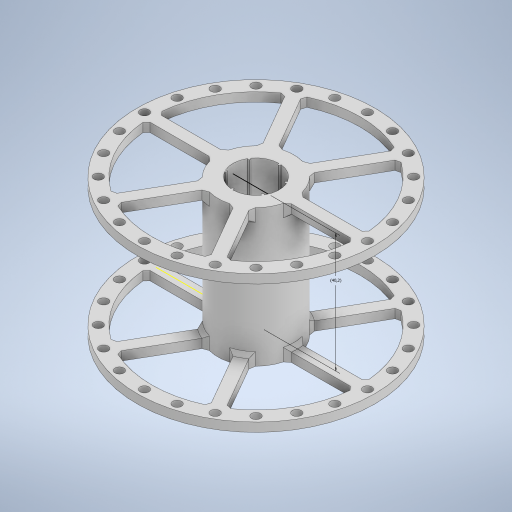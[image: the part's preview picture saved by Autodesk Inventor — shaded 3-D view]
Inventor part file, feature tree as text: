
AUTODESK INVENTOR PART (.ipt)
format: ipt  version: 2024 (Build 280153000, 153)  size: 560,128 bytes
history: native  units: mm
features: sketch x6, extrude x5, pattern_circular x3, chamfer x2, mirror x2, fillet x1
ambient origin geometry x8: Origin, YZ Plane, XZ Plane, XY Plane, X Axis, Y Axis, Z Axis, Center Point
bodies: Volumenkörper1 (feature_tree)
feature tree (19):
  extrude  "Extrusion1"  Depth=25.5mm
  extrude  "Extrusion2"  Depth=46.2mm
  extrude  "Extrusion4"  Depth=3.0mm TaperAngle=0.0deg
  chamfer  "Fasen1"  Distance=3.0mm
  mirror  "Spiegeln2"
  pattern_circular  "Runde Anordnung2"  Count=6 Angle=360.0deg
  chamfer  "Fasen2"  Distance=1.25mm Angle=45.0deg
  extrude  "Extrusion5"  Depth=3.0mm
  pattern_circular  "Runde Anordnung3"  [2 undecoded]
  mirror  "Spiegeln3"
  extrude  "Extrusion6"  Depth=0.35mm TaperAngle=360.0deg
  pattern_circular  "Runde Anordnung4"  [2 undecoded]
  fillet  "Rundung1"  Radius=0.75mm
  sketch  "Skizze7"  dims[d24=1.25mm d25=2.0mm d26=45.0deg d27=60.0mm d28=360.0deg d30=1.25mm d31=2.0mm d32=45.0deg d33=3.0mm d34=3.0mm d35=0.0mm d36=240.0mm d37=360.0deg d39=0.63mm d40=0.75mm d41=46.2mm d42=0.0mm d43=60.0mm d44=360.0deg d46=0.35mm d47=40.2mm]
  sketch  "Skizze1"  dims[d2=15.5mm d3=25.5mm]
  sketch  "Skizze3"  dims[d4=46.2mm d5=0.0mm d6=70.0mm]
  sketch  "Skizze4"  dims[d7=80.0mm d8=3.0mm d9=0.0mm]
  sketch  "Skizze5"  dims[d13=0.3mm]
  sketch  "Skizze6"  dims[d21=2.0mm d22=3.0mm d23=0.0mm]
note: 4 required parameter values undecoded (feature->parameter linkage not recoverable at this tier; creation-order binding heuristic only, values carry confidence <= 0.55)
